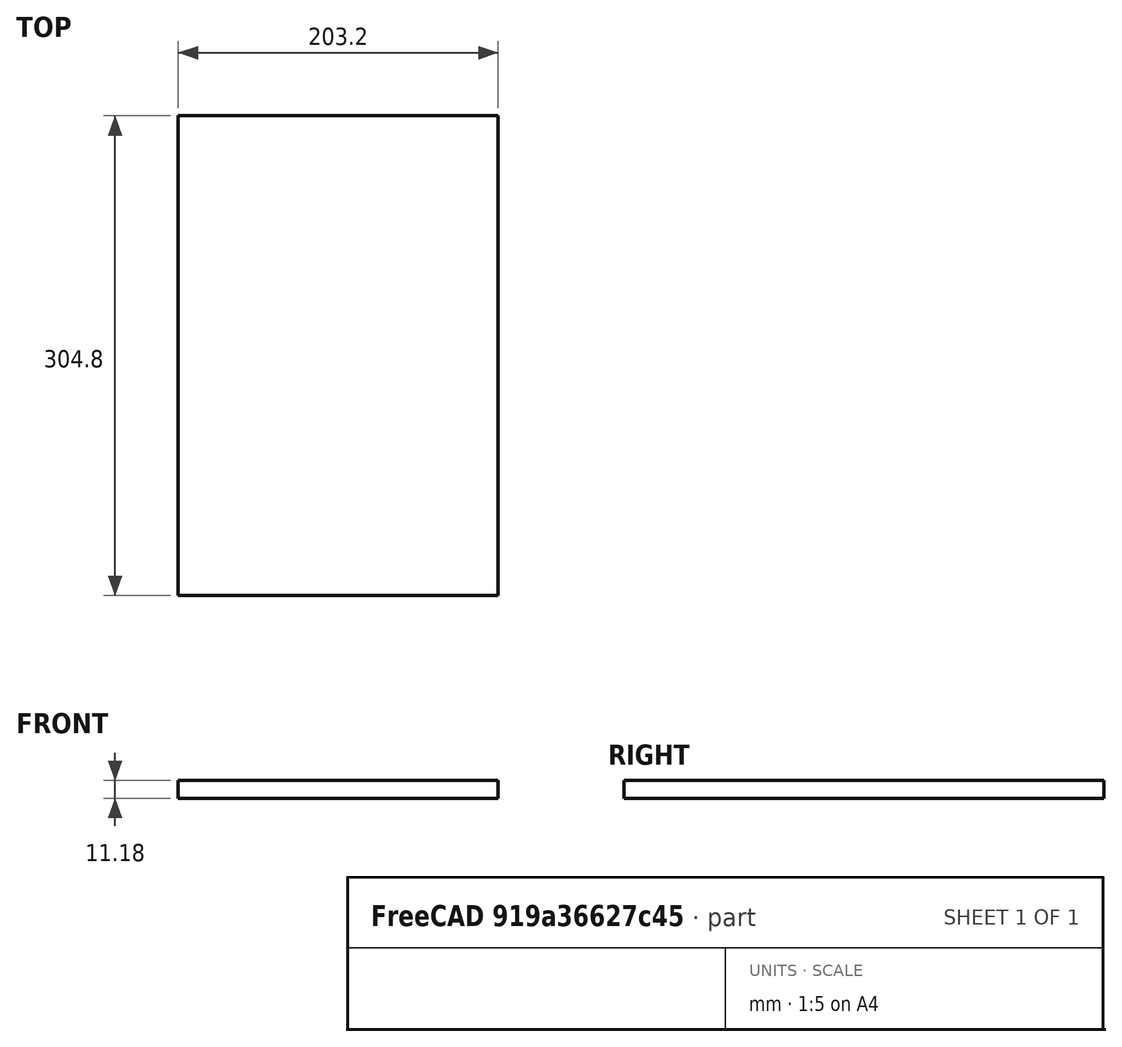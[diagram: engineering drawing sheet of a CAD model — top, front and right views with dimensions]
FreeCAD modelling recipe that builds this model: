
FCSTD DOCUMENT  (FreeCAD 0.16RUnknown)
Label: Top
License: All rights reserved
LicenseURL: http://en.wikipedia.org/wiki/All_rights_reserved
objects: Sketcher::SketchObject×1, Part::Box×1
note: 2 computed .brp shape members not serialized (recipe doc carries the construction recipe); baked Part::Feature solids carry a one-line shape summary decoded from their .brp

FEATURE [Sketcher::SketchObject] Sketch
  sketch-geometry (4):
    g0: LineSegment StartX=0 StartY=0 StartZ=0 EndX=304.8 EndY=0 EndZ=0
    g1: LineSegment StartX=304.8 StartY=0 StartZ=0 EndX=304.8 EndY=254 EndZ=0
    g2: LineSegment StartX=304.8 StartY=254 StartZ=0 EndX=0 EndY=254 EndZ=0
    g3: LineSegment StartX=0 StartY=254 StartZ=0 EndX=0 EndY=0 EndZ=0
  constraints (11):
    c: Coincident(g0,g1)
    c: Coincident(g1,g2)
    c: Coincident(g2,g3)
    c: Coincident(g3,g0)
    c: Horizontal(g0)
    c: Horizontal(g2)
    c: Vertical(g1)
    c: Vertical(g3)
    c: Coincident(g0,g-1)
    c: DistanceX(g0,g0) = 304.8
    c: DistanceY(g3,g3) = 254
FEATURE [Part::Box] Box  label="Cube"
  Height = 11.176
  Length = 203.2
  Width = 304.8
